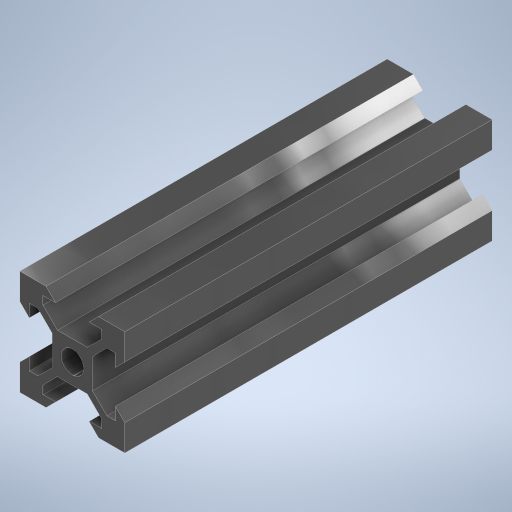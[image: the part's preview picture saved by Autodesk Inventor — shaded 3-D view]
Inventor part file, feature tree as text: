
AUTODESK INVENTOR PART (.ipt)
format: ipt  version: 2024.2 (Build 282272000, 272)  size: 316,928 bytes
history: native  units: mm
features: extrude x1, sketch x1
ambient origin geometry x8: Origin, YZ Plane, XZ Plane, XY Plane, X Axis, Y Axis, Z Axis, Center Point
bodies: Solid1 (feature_tree)
feature tree (2):
  extrude  "Extrusion1"  Depth=70.0mm
  sketch  "Sketch1"  dims[d16=10.0mm d19=3.2mm d21=4.4mm d22=4.4mm d24=45.0deg d25=1.8mm d27=1.8mm d28=45.0deg d29=3.2mm d31=1.4mm d33=2.15mm d34=3.825mm d35=3.825mm d36=135.0deg d37=40.0mm d39=360.0deg d41=70.0mm d42=0.0mm]
